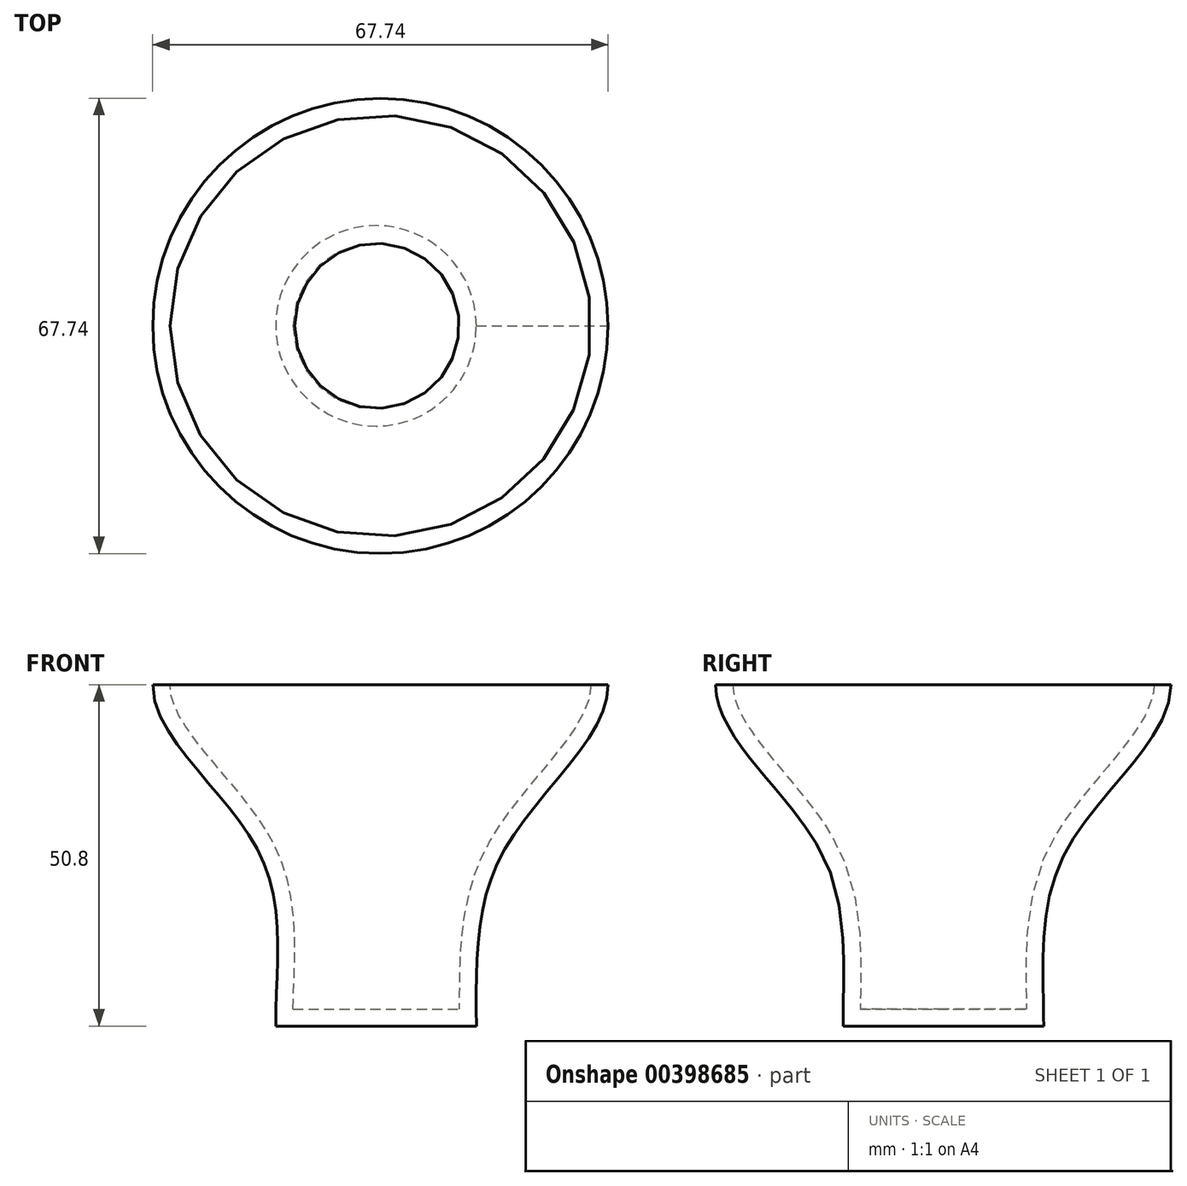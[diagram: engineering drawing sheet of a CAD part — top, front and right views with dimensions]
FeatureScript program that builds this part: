
annotation { "Feature Type Name" : "Feature", "Feature Type Description" : "" }
export const myFeature = defineFeature(function(context is Context, id is Id, definition is map)
    precondition{}
    {
        {
            var Q0;
            Q0=qCreatedBy(makeId("Top.planeOp"),FACE);
            cPlane(context, id + "F0", {"entities" : qUnion([Q0]), "cplaneType" : CPlaneType.OFFSET, "offset" : 25.4 * mm, "width" : 152.4 * mm, "height" : 152.4 * mm});
        }
        {
            var Q0;
            Q0=qCreatedBy(id+"F0.planeOp",FACE);
            cPlane(context, id + "F1", {"entities" : qUnion([Q0]), "cplaneType" : CPlaneType.OFFSET, "offset" : 25.4 * mm, "width" : 152.4 * mm, "height" : 152.4 * mm});
        }
        {
            var Q0;
            Q0=qCreatedBy(makeId("Top.planeOp"),FACE);
            var sketch = newSketch(context, id + "F2", { "sketchPlane" : qUnion([Q0])});
            skCircle(sketch, "E0", {"center": v(-39.59, 0) * mm, "radius": 14.92 * mm});
            skSolve(sketch);
        }
        {
            var Q0;
            Q0=qCreatedBy(id+"F0.planeOp",FACE);
            var sketch = newSketch(context, id + "F3", { "sketchPlane" : qUnion([Q0])});
            skCircle(sketch, "E1", {"center": v(-38.87, 0) * mm, "radius": 17.92 * mm});
            skSolve(sketch);
        }
        {
            var Q0;
            Q0=qCreatedBy(id+"F1.planeOp",FACE);
            var sketch = newSketch(context, id + "F4", { "sketchPlane" : qUnion([Q0])});
            skCircle(sketch, "E2", {"center": v(-38.94, 0) * mm, "radius": 33.87 * mm});
            skSolve(sketch);
        }
        {
            var Q0;
            Q0 = qSketchRegion(id + "F2", true);
            var Q1;
            Q1 = qSketchRegion(id + "F3", true);
            var Q2;
            Q2 = qSketchRegion(id + "F4", true);
            loft(context, id + "F5", {"startCondition" : LoftEndDerivativeType.NORMAL_TO_PROFILE, "startMagnitude" : 1, "endCondition" : LoftEndDerivativeType.NORMAL_TO_PROFILE, "endMagnitude" : 1, "sheetProfilesArray" : [{ "sheetProfileEntities" : qUnion([Q0]) }, { "sheetProfileEntities" : qUnion([Q1]) }, { "sheetProfileEntities" : qUnion([Q2]) }]});
        }
        {
            var Q0;
            Q0=makeQuery(id+"F5.opLoft","CAP_FACE",FACE,{"disambiguationData":[OSD([makeQuery(id+"F4.imprint","IMPRINT",FACE,{"disambiguationData":[TD([[makeQuery(id+"F4.imprint","IMPRINT",EDGE,{"derivedFrom":sQuery(id+"F4.wireOp",EDGE,"E2")}),1.0]])]})])],"isStart":true});
            shell(context, id + "F6", {"entities" : qUnion([Q0]), "thickness" : 2.54 * mm});
        }
    });
